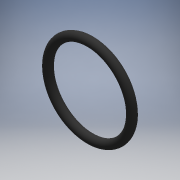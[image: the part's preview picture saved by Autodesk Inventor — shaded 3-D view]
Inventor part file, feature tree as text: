
AUTODESK INVENTOR PART (.ipt)
format: ipt  version: 2018 (Build 220112000, 112)  size: 126,464 bytes
history: native  units: mm
features: revolve x1, sketch x1
ambient origin geometry x8: Origin, YZ Plane, XZ Plane, XY Plane, X Axis, Y Axis, Z Axis, Center Point
bodies: Solid1 (feature_tree)
feature tree (2):
  revolve  "Revolution1"  [1 undecoded]
  sketch  "Sketch1"  dims[d0=3.5mm d1=17.5mm d2=90.0deg]
note: 1 required parameter value undecoded (feature->parameter linkage not recoverable at this tier; creation-order binding heuristic only, values carry confidence <= 0.55)
